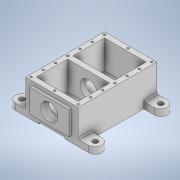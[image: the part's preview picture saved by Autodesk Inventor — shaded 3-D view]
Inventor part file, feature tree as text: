
AUTODESK INVENTOR PART (.ipt)
format: ipt  version: 2022 (Build 260153000, 153)  size: 253,952 bytes
history: native  units: mm
features: sketch x8, extrude x6, pattern_linear x3, fillet x2, hole x2, other x1, projected_geometry x1
ambient origin geometry x8: Origin, YZ Plane, XZ Plane, XY Plane, X Axis, Y Axis, Z Axis, Center Point
bodies: Body1 (feature_tree)
feature tree (23):
  other  "Твердое тело1"
  extrude  "Выдавливание1"  Depth=200.0mm
  extrude  "Выдавливание2"  Depth=300.0mm
  fillet  "Сопряжение1"  Radius=130.0mm
  extrude  "Выдавливание3"  Depth=100.0mm
  extrude  "Выдавливание4"  Depth=6.0mm
  extrude  "Выдавливание5"  Depth=50.0mm
  extrude  "Выдавливание7"  TaperAngle=0.0deg  [1 undecoded]
  fillet  "Сопряжение2"  Radius=5.0mm
  hole  "Отверстие1"  [1 undecoded]
  pattern_linear  "Прямоуг.массив1"  Count1=11 Spacing1=0.0mm
  pattern_linear  "Прямоуг.массив2"  Spacing1=15.0mm  [1 undecoded]
  pattern_linear  "Прямоуг.массив3"  Spacing1=25.0mm  [1 undecoded]
  hole  "Отверстие2"  [1 undecoded]
  sketch  "Эскиз1"
  sketch  "Эскиз2"
  sketch  "Эскиз3"
  sketch  "Эскиз4"
  sketch  "Эскиз5"
  projected_geometry  "Спроецированная петля1"
  sketch  "Эскиз6"
  sketch  "Эскиз7"
  sketch  "Эскиз8"
note: 5 required parameter values undecoded (feature->parameter linkage not recoverable at this tier; creation-order binding heuristic only, values carry confidence <= 0.55)
